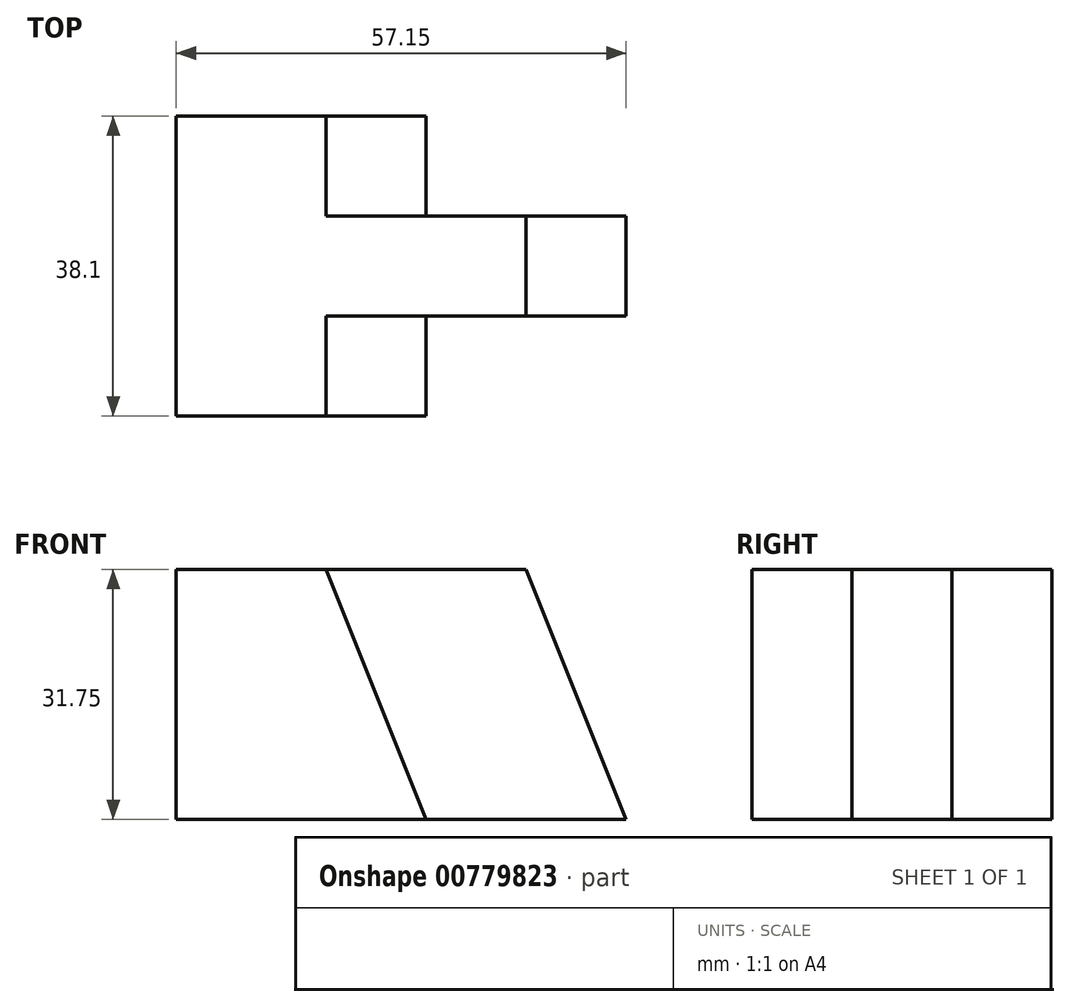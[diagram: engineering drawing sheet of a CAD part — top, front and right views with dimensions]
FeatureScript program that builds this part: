
annotation { "Feature Type Name" : "Feature", "Feature Type Description" : "" }
export const myFeature = defineFeature(function(context is Context, id is Id, definition is map)
    precondition{}
    {
        {
            var Q0;
            Q0=qCreatedBy(makeId("Top.planeOp"),FACE);
            var sketch = newSketch(context, id + "F0", { "sketchPlane" : qUnion([Q0])});
            skLineSegment(sketch, "E0", {"start": v(0, 0) * mm, "end": v(0, 38.1) * mm});
            skLineSegment(sketch, "E1", {"start": v(0, 38.1) * mm, "end": v(31.75, 38.1) * mm});
            skLineSegment(sketch, "E2", {"start": v(31.75, 38.1) * mm, "end": v(31.75, 25.4) * mm});
            skLineSegment(sketch, "E3", {"start": v(31.75, 25.4) * mm, "end": v(57.15, 25.4) * mm});
            skLineSegment(sketch, "E4", {"start": v(57.15, 25.4) * mm, "end": v(57.15, 12.7) * mm});
            skLineSegment(sketch, "E5", {"start": v(57.15, 12.7) * mm, "end": v(31.75, 12.7) * mm});
            skLineSegment(sketch, "E6", {"start": v(31.75, 12.7) * mm, "end": v(31.75, 0) * mm});
            skLineSegment(sketch, "E7", {"start": v(31.75, 0) * mm, "end": v(0, 0) * mm});
            skSolve(sketch);
        }
        {
            var Q0;
            Q0 = qSketchRegion(id + "F0", true);
            extrude(context, id + "F1", {"entities" : qUnion([Q0]), "depth" : 31.75 * mm, "offsetDistance" : 25.4 * mm});
        }
        {
            var Q0;
            Q0=makeQuery(id+"F1.opExtrude","SWEPT_FACE",FACE,{"disambiguationData":[OSD([sQuery(id+"F0.wireOp",EDGE,"E1")])]});
            var sketch = newSketch(context, id + "F2", { "sketchPlane" : qUnion([Q0])});
            skLineSegment(sketch, "E8", {"start": v(0, 31.75) * mm, "end": v(-19.05, 31.75) * mm});
            skLineSegment(sketch, "E9", {"start": v(-19.05, 31.75) * mm, "end": v(-31.75, 0) * mm});
            skSolve(sketch);
        }
        {
            var Q0;
            Q0 = qSketchRegion(id + "F2", true);
            var Q1;
            {var subQ0=sQuery(id+"F2.wireOp",EDGE,"E9");Q1=makeQuery(id+"F2.imprint","IMPRINT",FACE,{"disambiguationData":[TD([[makeQuery(id+"F2.imprint","IMPRINT",EDGE,{"derivedFrom":subQ0}),-1.0]])]});}
            extrude(context, id + "F3", {"entities" : qUnion([Q0, Q1]), "operationType" : NewBodyOperationType.REMOVE, "oppositeDirection" : true, "depth" : 12.7 * mm, "offsetDistance" : 25.4 * mm});
        }
        {
            var Q0;
            Q0=makeQuery(id+"F3.boolean.opBoolean","MERGE",FACE,{"derivedFrom":[makeQuery(id+"F1.opExtrude","SWEPT_FACE",FACE,{"disambiguationData":[OSD([sQuery(id+"F0.wireOp",EDGE,"E3")])]}),makeQuery(id+"F3.opExtrude","CAP_FACE",FACE,{"disambiguationData":[OSD([sQuery(id+"F0.wireOp",EDGE,"E1"),sQuery(id+"F0.wireOp",EDGE,"E2"),sQuery(id+"F2.wireOp",EDGE,"E9")])],"isStart":false})]});
            var sketch = newSketch(context, id + "F4", { "sketchPlane" : qUnion([Q0])});
            skLineSegment(sketch, "E10", {"start": v(-57.15, 31.75) * mm, "end": v(-44.45, 31.75) * mm});
            skLineSegment(sketch, "E11", {"start": v(-44.45, 31.75) * mm, "end": v(-57.15, 0) * mm});
            skSolve(sketch);
        }
        {
            var Q0;
            Q0 = qSketchRegion(id + "F4", true);
            var Q1;
            Q1=makeQuery(id+"F4.imprint","IMPRINT",FACE,{"disambiguationData":[TD([[makeQuery(id+"F4.imprint","IMPRINT",EDGE,{"derivedFrom":sQuery(id+"F4.wireOp",EDGE,"E10")}),1.0]])]});
            extrude(context, id + "F5", {"entities" : qUnion([Q0, Q1]), "operationType" : NewBodyOperationType.REMOVE, "oppositeDirection" : true, "depth" : 12.7 * mm, "offsetDistance" : 25.4 * mm});
        }
        {
            var Q0;
            Q0=makeQuery(id+"F1.opExtrude","SWEPT_FACE",FACE,{"disambiguationData":[OSD([sQuery(id+"F0.wireOp",EDGE,"E7")])]});
            var sketch = newSketch(context, id + "F6", { "sketchPlane" : qUnion([Q0])});
            skLineSegment(sketch, "E12", {"start": v(0, 31.75) * mm, "end": v(19.05, 31.75) * mm});
            skLineSegment(sketch, "E13", {"start": v(19.05, 31.75) * mm, "end": v(31.75, 0) * mm});
            skSolve(sketch);
        }
        {
            var Q0;
            Q0 = qSketchRegion(id + "F6", true);
            var Q1;
            {var subQ0=sQuery(id+"F6.wireOp",EDGE,"E13");Q1=makeQuery(id+"F6.imprint","IMPRINT",FACE,{"disambiguationData":[TD([[makeQuery(id+"F6.imprint","IMPRINT",EDGE,{"derivedFrom":subQ0}),1.0]])]});}
            extrude(context, id + "F7", {"entities" : qUnion([Q0, Q1]), "operationType" : NewBodyOperationType.REMOVE, "oppositeDirection" : true, "depth" : 12.7 * mm, "offsetDistance" : 25.4 * mm});
        }
    });
